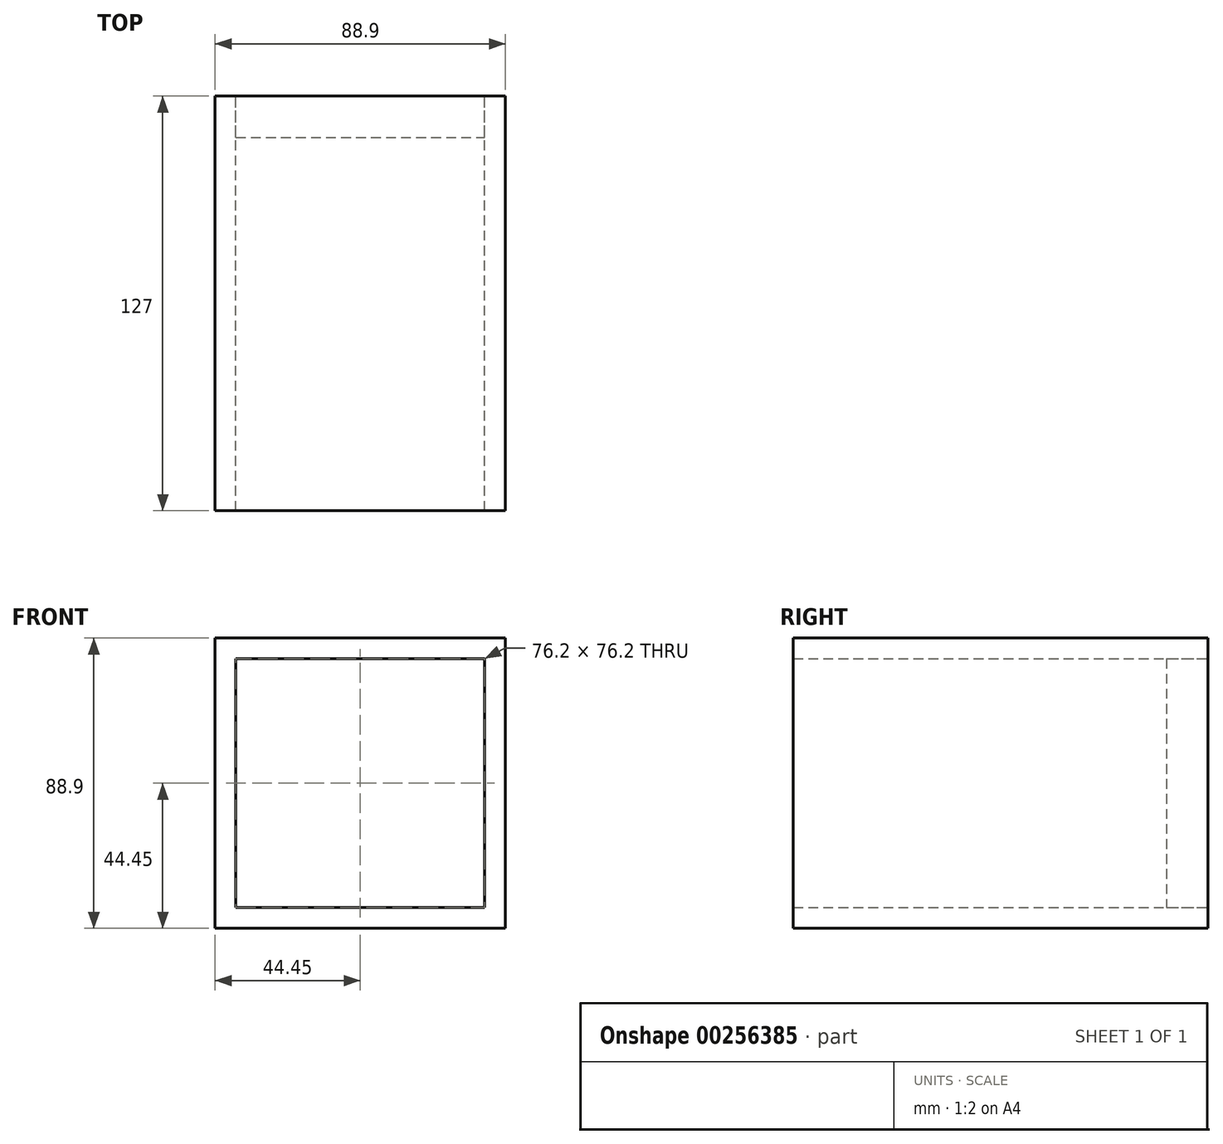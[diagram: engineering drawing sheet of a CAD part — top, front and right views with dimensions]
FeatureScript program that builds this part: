
annotation { "Feature Type Name" : "Feature", "Feature Type Description" : "" }
export const myFeature = defineFeature(function(context is Context, id is Id, definition is map)
    precondition{}
    {
        {
            var Q0;
            Q0=qCreatedBy(makeId("Front.planeOp"),FACE);
            var sketch = newSketch(context, id + "F0", { "sketchPlane" : qUnion([Q0])});
            skLineSegment(sketch, "E0.bottom", {"start": v(-44.45, 44.45) * mm, "end": v(44.45, 44.45) * mm});
            skLineSegment(sketch, "E0.top", {"start": v(-44.45, -44.45) * mm, "end": v(44.45, -44.45) * mm});
            skLineSegment(sketch, "E0.left", {"start": v(-44.45, 44.45) * mm, "end": v(-44.45, -44.45) * mm});
            skLineSegment(sketch, "E0.right", {"start": v(44.45, 44.45) * mm, "end": v(44.45, -44.45) * mm});
            skPoint(sketch, "E0.middle", {"position": v(0, 0) * mm});
            skLineSegment(sketch, "E1.bottom", {"start": v(-38.1, 38.1) * mm, "end": v(38.1, 38.1) * mm});
            skLineSegment(sketch, "E1.top", {"start": v(-38.1, -38.1) * mm, "end": v(38.1, -38.1) * mm});
            skLineSegment(sketch, "E1.left", {"start": v(-38.1, 38.1) * mm, "end": v(-38.1, -38.1) * mm});
            skLineSegment(sketch, "E1.right", {"start": v(38.1, 38.1) * mm, "end": v(38.1, -38.1) * mm});
            skSolve(sketch);
        }
        {
            var Q0;
            Q0=makeQuery(id+"F0.imprint","IMPRINT",FACE,{"disambiguationData":[TD([[makeQuery(id+"F0.imprint","IMPRINT",EDGE,{"derivedFrom":sQuery(id+"F0.wireOp",EDGE,"E0.bottom")}),-1.0]])]});
            extrude(context, id + "F1", {"entities" : qUnion([Q0]), "depth" : 127 * mm});
        }
        {
            var Q0;
            Q0=makeQuery(id+"F0.imprint","IMPRINT",FACE,{"disambiguationData":[TD([[makeQuery(id+"F0.imprint","IMPRINT",EDGE,{"derivedFrom":sQuery(id+"F0.wireOp",EDGE,"E1.bottom")}),-1.0]])]});
            extrude(context, id + "F2", {"entities" : qUnion([Q0]), "depth" : 12.7 * mm});
        }
    });
